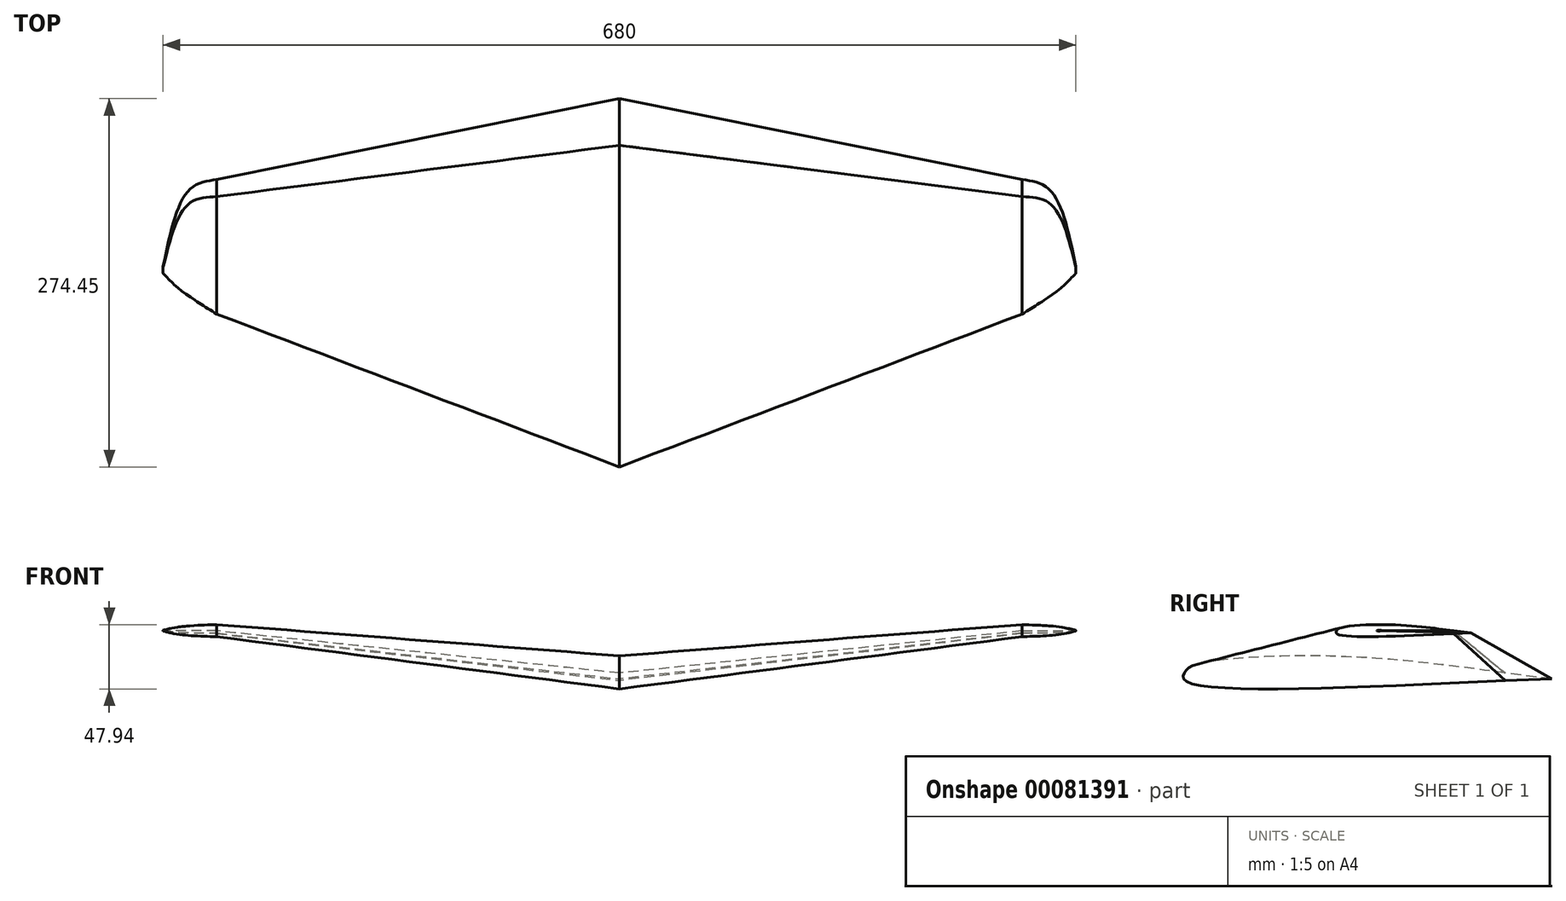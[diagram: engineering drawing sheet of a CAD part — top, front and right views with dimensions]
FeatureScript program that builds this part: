
annotation { "Feature Type Name" : "Feature", "Feature Type Description" : "" }
export const myFeature = defineFeature(function(context is Context, id is Id, definition is map)
    precondition{}
    {
        {
            var Q0;
            Q0=qCreatedBy(makeId("Right.planeOp"),FACE);
            cPlane(context, id + "F0", {"entities" : qUnion([Q0]), "cplaneType" : CPlaneType.OFFSET, "offset" : 300 * mm, "width" : 150 * mm, "height" : 150 * mm});
        }
        {
            var Q0;
            Q0=qCreatedBy(makeId("Right.planeOp"),FACE);
            var sketch = newSketch(context, id + "F1", { "sketchPlane" : qUnion([Q0])});
            skLineSegment(sketch, "E0", {"start": v(177.88, 0) * mm, "end": v(143.04, 4.36) * mm});
            skLineSegment(sketch, "E1", {"start": v(177.88, 0) * mm, "end": v(143.5, -1.15) * mm});
            skFitSpline(sketch, "E2", {"points": [v(143.04, 4.36) * mm, v(90.31, 11.23) * mm, v(-4.58, 17.2) * mm, v(-89.4, 9.86) * mm, v(-95.82, 4.36) * mm, v(-95.36, -1.15) * mm, v(143.5, -1.15) * mm], "startDerivative": vector(-318.71, 44.7) * mm, "endDerivative": vector(1034.8, 50.16) * mm});
            skSolve(sketch);
        }
        {
            var Q0;
            Q0=qCreatedBy(id+"F0.planeOp",FACE);
            var sketch = newSketch(context, id + "F2", { "sketchPlane" : qUnion([Q0])});
            skLineSegment(sketch, "E3", {"start": v(117.6, 34.16) * mm, "end": v(104.87, 35.75) * mm});
            skLineSegment(sketch, "E4", {"start": v(117.6, 34.16) * mm, "end": v(105.04, 33.74) * mm});
            skFitSpline(sketch, "E5", {"points": [v(104.87, 35.75) * mm, v(85.6, 38.26) * mm, v(50.93, 40.44) * mm, v(19.94, 37.76) * mm, v(17.6, 35.75) * mm, v(17.77, 33.74) * mm, v(105.04, 33.74) * mm], "startDerivative": vector(-116.45, 16.33) * mm, "endDerivative": vector(378.08, 18.33) * mm});
            skSolve(sketch);
        }
        {
            var Q0;
            Q0=qCreatedBy(makeId("Right.planeOp"),FACE);
            cPlane(context, id + "F3", {"entities" : qUnion([Q0]), "cplaneType" : CPlaneType.OFFSET, "offset" : 320 * mm, "width" : 150 * mm, "height" : 150 * mm});
        }
        {
            var Q0;
            Q0=qCreatedBy(id+"F3.planeOp",FACE);
            var sketch = newSketch(context, id + "F4", { "sketchPlane" : qUnion([Q0])});
            skLineSegment(sketch, "E6", {"start": v(110.32, 34.47) * mm, "end": v(100.14, 35.74) * mm});
            skLineSegment(sketch, "E7", {"start": v(110.32, 34.47) * mm, "end": v(100.27, 34.13) * mm});
            skFitSpline(sketch, "E8", {"points": [v(100.14, 35.74) * mm, v(84.73, 37.75) * mm, v(57, 39.5) * mm, v(32.2, 37.35) * mm, v(30.32, 35.74) * mm, v(30.46, 34.13) * mm, v(100.27, 34.13) * mm], "startDerivative": vector(-93.16, 13.07) * mm, "endDerivative": vector(302.47, 14.66) * mm});
            skSolve(sketch);
        }
        {
            var Q0;
            Q0=qCreatedBy(makeId("Right.planeOp"),FACE);
            cPlane(context, id + "F5", {"entities" : qUnion([Q0]), "cplaneType" : CPlaneType.OFFSET, "offset" : 340 * mm, "width" : 150 * mm, "height" : 150 * mm});
        }
        {
            var Q0;
            Q0=qCreatedBy(id+"F5.planeOp",FACE);
            var sketch = newSketch(context, id + "F6", { "sketchPlane" : qUnion([Q0])});
            skLineSegment(sketch, "E9", {"start": v(52.73, 35.85) * mm, "end": v(52.1, 35.93) * mm});
            skLineSegment(sketch, "E10", {"start": v(52.73, 35.85) * mm, "end": v(52.1, 35.83) * mm});
            skFitSpline(sketch, "E11", {"points": [v(52.1, 35.93) * mm, v(51.13, 36.05) * mm, v(49.4, 36.16) * mm, v(47.85, 36.03) * mm, v(47.73, 35.93) * mm, v(47.74, 35.83) * mm, v(52.1, 35.83) * mm], "startDerivative": vector(-5.82, 0.82) * mm, "endDerivative": vector(18.9, 0.92) * mm});
            skSolve(sketch);
        }
        {
            var Q0;
            Q0 = qSketchRegion(id + "F2", true);
            var Q1;
            Q1 = qSketchRegion(id + "F4", true);
            var Q2;
            Q2 = qSketchRegion(id + "F6", true);
            loft(context, id + "F7", {"sheetProfilesArray" : [{ "sheetProfileEntities" : qUnion([Q0]) }, { "sheetProfileEntities" : qUnion([Q1]) }, { "sheetProfileEntities" : qUnion([Q2]) }]});
        }
        {
            var Q1;
            Q1 = qSketchRegion(id + "F2", true);
            var Q2;
            Q2 = qSketchRegion(id + "F1", true);
            loft(context, id + "F8", {"operationType" : NewBodyOperationType.ADD, "sheetProfilesArray" : [{ "sheetProfileEntities" : qUnion([Q1]) }, { "sheetProfileEntities" : qUnion([Q2]) }]});
        }
        {
            var Q0;
            Q0=makeQuery(id+"F7.opLoft","SWEPT_BODY",BODY,{"disambiguationData":[OSD([makeQuery(id+"F2.imprint","IMPRINT",FACE,{"disambiguationData":[TD([[makeQuery(id+"F2.imprint","IMPRINT",EDGE,{"derivedFrom":sQuery(id+"F2.wireOp",EDGE,"E3")}),1.0]])]}),sQuery(id+"F4.wireOp",EDGE,"E6"),makeQuery(id+"F6.imprint","IMPRINT",FACE,{"disambiguationData":[TD([[makeQuery(id+"F6.imprint","IMPRINT",EDGE,{"derivedFrom":sQuery(id+"F6.wireOp",EDGE,"E9")}),1.0]])]})])]});
            var Q1;
            Q1=qCreatedBy(makeId("Right.planeOp"),FACE);
            mirror(context, id + "F9", {"operationType" : NewBodyOperationType.ADD, "entities" : qUnion([Q0]), "mirrorPlane" : qUnion([Q1])});
        }
    });
